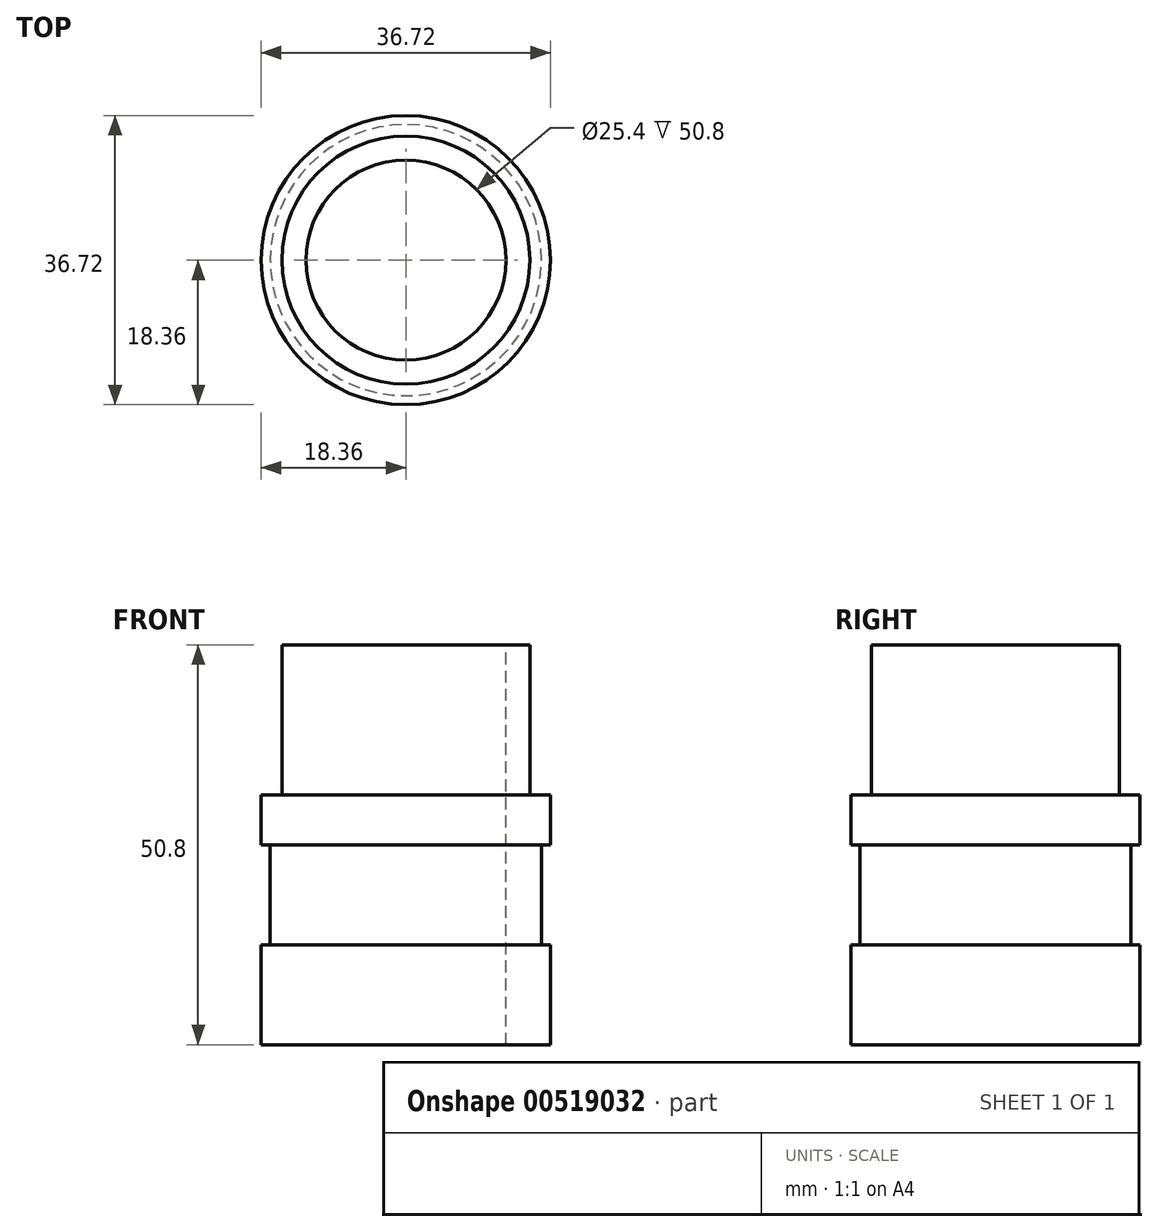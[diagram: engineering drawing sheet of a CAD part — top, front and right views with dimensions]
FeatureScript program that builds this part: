
annotation { "Feature Type Name" : "Feature", "Feature Type Description" : "" }
export const myFeature = defineFeature(function(context is Context, id is Id, definition is map)
    precondition{}
    {
        {
            var Q0;
            Q0=qCreatedBy(makeId("Front.planeOp"),FACE);
            var sketch = newSketch(context, id + "F0", { "sketchPlane" : qUnion([Q0])});
            skLineSegment(sketch, "E0", {"start": v(0, 11.12) * mm, "end": v(0, 0) * mm});
            skSolve(sketch);
        }
        {
            var Q0;
            Q0=qCreatedBy(makeId("Front.planeOp"),FACE);
            var sketch = newSketch(context, id + "F1", { "sketchPlane" : qUnion([Q0])});
            skLineSegment(sketch, "E1", {"start": v(12.7, 50.8) * mm, "end": v(12.7, 0) * mm});
            skLineSegment(sketch, "E2", {"start": v(12.7, 0) * mm, "end": v(18.36, 0) * mm});
            skLineSegment(sketch, "E3", {"start": v(18.36, 0) * mm, "end": v(18.36, 12.7) * mm});
            skLineSegment(sketch, "E4", {"start": v(15.75, 50.8) * mm, "end": v(12.7, 50.8) * mm});
            skLineSegment(sketch, "E5", {"start": v(18.36, 31.75) * mm, "end": v(18.36, 25.4) * mm});
            skLineSegment(sketch, "E6", {"start": v(18.36, 25.4) * mm, "end": v(17.22, 25.4) * mm});
            skLineSegment(sketch, "E7", {"start": v(17.22, 12.7) * mm, "end": v(18.36, 12.7) * mm});
            skLineSegment(sketch, "E8.trimOffspring", {"start": v(18.36, 25.4) * mm, "end": v(18.36, 31.75) * mm});
            skLineSegment(sketch, "E9", {"start": v(17.22, 25.4) * mm, "end": v(17.22, 12.7) * mm});
            skLineSegment(sketch, "E10", {"start": v(15.75, 31.75) * mm, "end": v(15.75, 50.8) * mm});
            skLineSegment(sketch, "E11", {"start": v(15.75, 31.75) * mm, "end": v(18.36, 31.75) * mm});
            skSolve(sketch);
        }
        {
            var Q0;
            Q0=makeQuery(id+"F1.imprint","IMPRINT",FACE,{"disambiguationData":[TD([[makeQuery(id+"F1.imprint","IMPRINT",EDGE,{"derivedFrom":sQuery(id+"F1.wireOp",EDGE,"E1")}),1.0]])]});
            var Q1;
            Q1=sQuery(id+"F0.wireOp",EDGE,"E0");
            revolve(context, id + "F2", {"entities" : qUnion([Q0]), "axis" : qUnion([Q1]), "revolveType" : RevolveType.FULL});
        }
    });
